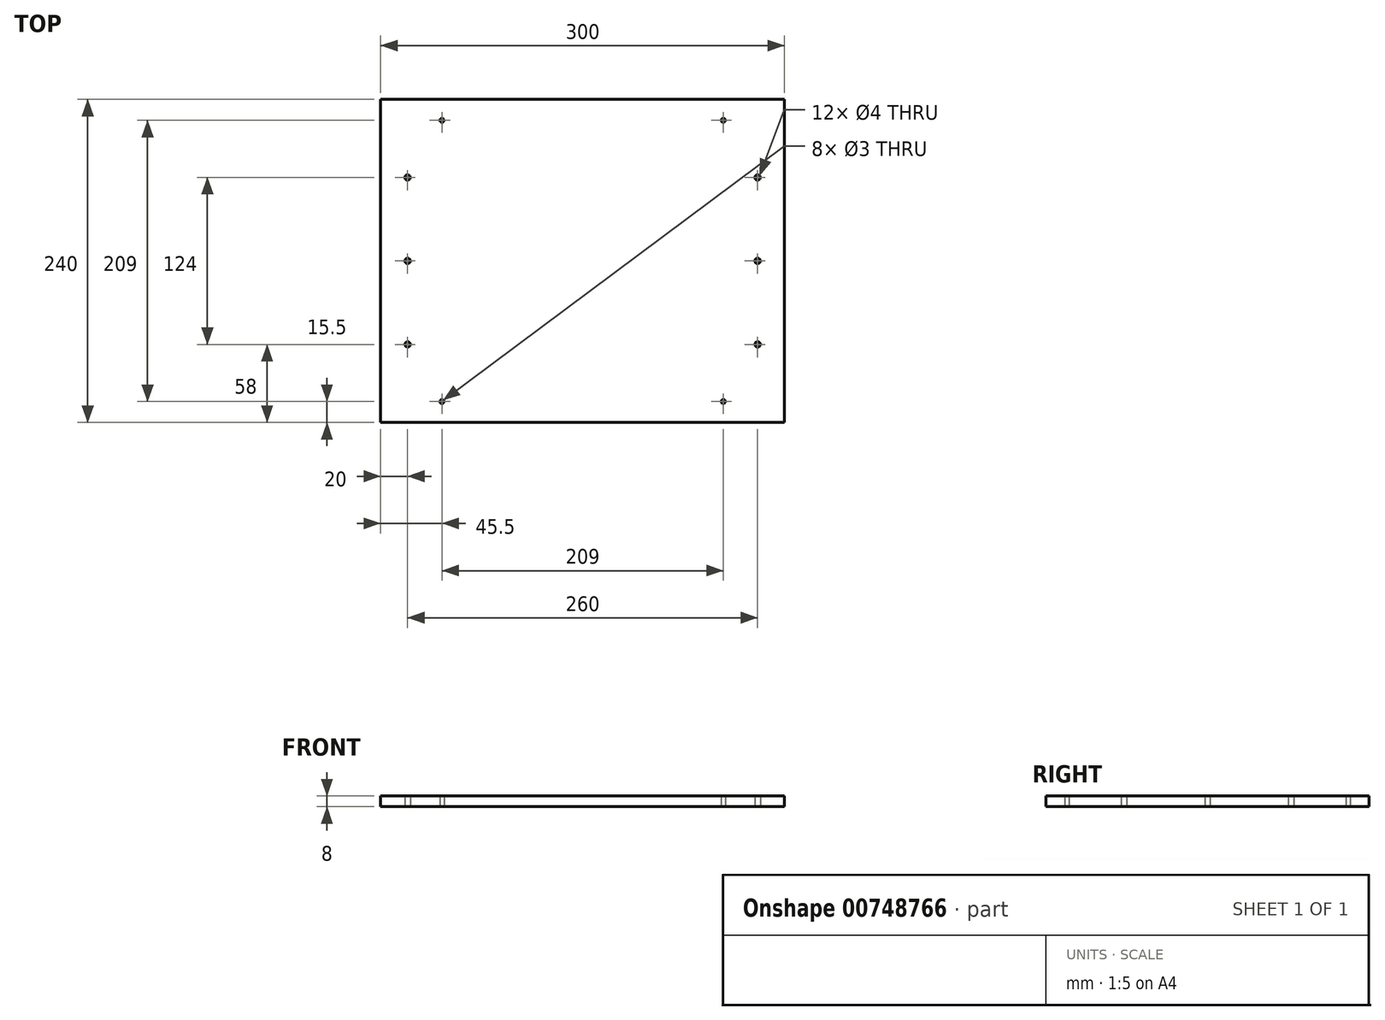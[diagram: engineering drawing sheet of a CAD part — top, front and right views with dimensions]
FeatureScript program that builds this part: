
annotation { "Feature Type Name" : "Feature", "Feature Type Description" : "" }
export const myFeature = defineFeature(function(context is Context, id is Id, definition is map)
    precondition{}
    {
        {
            var Q0;
            Q0=qCreatedBy(makeId("Top.planeOp"),FACE);
            var sketch = newSketch(context, id + "F0", { "sketchPlane" : qUnion([Q0])});
            skLineSegment(sketch, "E0.bottom", {"start": v(150, 120) * mm, "end": v(-150, 120) * mm});
            skLineSegment(sketch, "E0.top", {"start": v(150, -120) * mm, "end": v(-150, -120) * mm});
            skLineSegment(sketch, "E0.left", {"start": v(150, 120) * mm, "end": v(150, -120) * mm});
            skLineSegment(sketch, "E0.right", {"start": v(-150, 120) * mm, "end": v(-150, -120) * mm});
            skPoint(sketch, "E0.middle", {"position": v(0, 0) * mm});
            skCircle(sketch, "E1", {"center": v(-130, 0) * mm, "radius": 2 * mm});
            skCircle(sketch, "E2", {"center": v(130, 0) * mm, "radius": 2 * mm});
            skCircle(sketch, "E3", {"center": v(130, 62) * mm, "radius": 2 * mm});
            skCircle(sketch, "E4", {"center": v(130, -62) * mm, "radius": 2 * mm});
            skCircle(sketch, "E5", {"center": v(-130, -62) * mm, "radius": 2 * mm});
            skCircle(sketch, "E6", {"center": v(-130, 62) * mm, "radius": 2 * mm});
            skCircle(sketch, "E7", {"center": v(-104.5, -104.5) * mm, "radius": 1.5 * mm});
            skCircle(sketch, "E8", {"center": v(104.5, -104.5) * mm, "radius": 1.5 * mm});
            skCircle(sketch, "E9", {"center": v(104.5, 104.5) * mm, "radius": 1.5 * mm});
            skCircle(sketch, "E10", {"center": v(-104.5, 104.5) * mm, "radius": 1.5 * mm});
            skSolve(sketch);
        }
        {
            var Q0;
            Q0=makeQuery(id+"F0.imprint","IMPRINT",FACE,{"disambiguationData":[TD([[makeQuery(id+"F0.imprint","IMPRINT",EDGE,{"derivedFrom":sQuery(id+"F0.wireOp",EDGE,"E0.bottom")}),1.0]])]});
            extrude(context, id + "F1", {"entities" : qUnion([Q0]), "depth" : 8 * mm, "offsetDistance" : 25 * mm});
        }
    });
